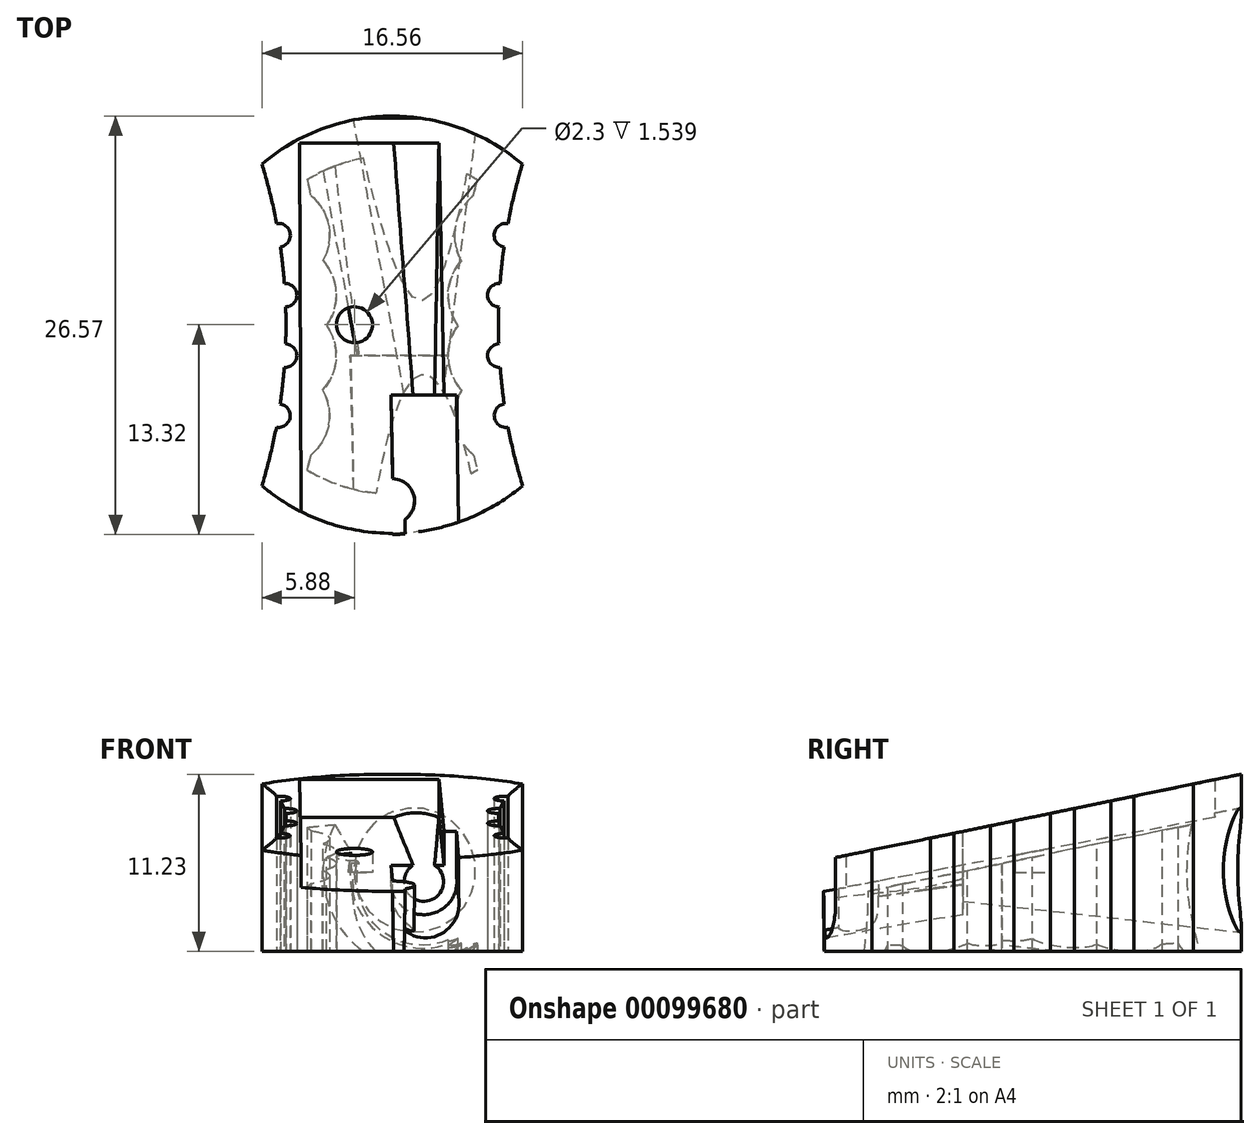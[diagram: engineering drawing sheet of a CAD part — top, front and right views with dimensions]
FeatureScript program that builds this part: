
annotation { "Feature Type Name" : "Feature", "Feature Type Description" : "" }
export const myFeature = defineFeature(function(context is Context, id is Id, definition is map)
    precondition{}
    {
        {
            var Q0;
            Q0=qCreatedBy(makeId("Top.planeOp"),FACE);
            var sketch = newSketch(context, id + "F0", { "sketchPlane" : qUnion([Q0])});
            skArc(sketch, "E0", {"start": v(-8.02, 9.64) * mm, "mid": v(-8.05, 9.61) * mm, "end": v(-8.09, 9.59) * mm, "construction": true});
            skArc(sketch, "E1", {"start": v(0, 13.25) * mm, "mid": v(-4.4, 12.46) * mm, "end": v(-8.27, 10.2) * mm});
            skArc(sketch, "E2", {"start": v(-8.28, -10.23) * mm, "mid": v(-6.76, 0.87) * mm, "end": v(-8.83, 11.88) * mm});
            skLineSegment(sketch, "E3", {"start": v(0, 27.52) * mm, "end": v(0, -29.67) * mm});
            skLineSegment(sketch, "E4", {"start": v(0, 13.25) * mm, "end": v(1.48, 13.25) * mm});
            skLineSegment(sketch, "E5", {"start": v(-7.8, 10.6) * mm, "end": v(-9.31, 9.42) * mm});
            skLineSegment(sketch, "E6", {"start": v(-9.2, 12.93) * mm, "end": v(-8.83, 11.88) * mm});
            skArc(sketch, "E7.trimOffspring", {"start": v(-8.28, -10.23) * mm, "mid": v(-4.4, -12.47) * mm, "end": v(0, -13.25) * mm});
            skLineSegment(sketch, "E8", {"start": v(0, -13.25) * mm, "end": v(1.48, -13.25) * mm});
            skCircle(sketch, "E9", {"center": v(-7.22, 5.69) * mm, "radius": 0.75 * mm});
            skCircle(sketch, "E10.1.0", {"center": v(-6.8, 1.88) * mm, "radius": 0.75 * mm});
            skCircle(sketch, "E10.2.0", {"center": v(-6.8, -1.96) * mm, "radius": 0.75 * mm});
            skCircle(sketch, "E10.3.0", {"center": v(-7.23, -5.77) * mm, "radius": 0.75 * mm});
            skLineSegment(sketch, "E10.anchor1", {"start": v(-41.75, 0) * mm, "end": v(-7.22, 5.69) * mm, "construction": true});
            skLineSegment(sketch, "E10.anchor2", {"start": v(-41.75, 0) * mm, "end": v(-7.23, -5.77) * mm, "construction": true});
            skSolve(sketch);
        }
        {
            var Q0;
            {var subQ3=sQuery(id+"F0.wireOp",EDGE,"E7.trimOffspring");Q0=makeQuery(id+"F0.imprint","IMPRINT",FACE,{"disambiguationData":[TD([[makeQuery(id+"F0.imprint","IMPRINT",EDGE,{"derivedFrom":subQ3}),1.0]])]});}
            extrude(context, id + "F1", {"entities" : qUnion([Q0]), "depth" : 11.23 * mm});
        }
        {
            var Q0;
            Q0=makeQuery(id+"F1.opExtrude","SWEPT_BODY",BODY,{"disambiguationData":[OSD([sQuery(id+"F0.wireOp",EDGE,"E1"),sQuery(id+"F0.wireOp",EDGE,"E2"),sQuery(id+"F0.wireOp",EDGE,"E3"),sQuery(id+"F0.wireOp",EDGE,"E7.trimOffspring")])]});
            var Q1;
            Q1=qCreatedBy(makeId("Right.planeOp"),FACE);
            mirror(context, id + "F2", {"operationType" : NewBodyOperationType.ADD, "entities" : qUnion([Q0]), "mirrorPlane" : qUnion([Q1])});
        }
        {
            var Q0;
            Q0=qCreatedBy(makeId("Right.planeOp"),FACE);
            var sketch = newSketch(context, id + "F3", { "sketchPlane" : qUnion([Q0])});
            skLineSegment(sketch, "E11", {"start": v(10.2, 10.63) * mm, "end": v(-10.23, 6.43) * mm});
            skLineSegment(sketch, "E12", {"start": v(15.76, 11.77) * mm, "end": v(-16.6, 5.12) * mm});
            skPoint(sketch, "E13.end.orphan", {"position": v(10.2, 0) * mm});
            skPoint(sketch, "E14.end.orphan", {"position": v(-10.23, 0) * mm});
            skLineSegment(sketch, "E15", {"start": v(15.76, 11.77) * mm, "end": v(15.76, 16.34) * mm});
            skLineSegment(sketch, "E16", {"start": v(15.76, 16.34) * mm, "end": v(-16.6, 16.34) * mm});
            skLineSegment(sketch, "E17", {"start": v(-16.6, 16.34) * mm, "end": v(-16.6, 5.12) * mm});
            skLineSegment(sketch, "E18", {"start": v(15.76, 11.77) * mm, "end": v(15.76, -3.68) * mm});
            skLineSegment(sketch, "E19", {"start": v(15.76, -3.68) * mm, "end": v(-16.6, -3.68) * mm});
            skLineSegment(sketch, "E20", {"start": v(-16.6, -3.68) * mm, "end": v(-16.6, 5.12) * mm});
            skSolve(sketch);
        }
        {
            var Q0;
            {var subQ0=sQuery(id+"F3.wireOp",EDGE,"E18");Q0=makeQuery(id+"F3.imprint","IMPRINT",FACE,{"disambiguationData":[TD([[makeQuery(id+"F3.imprint","IMPRINT",EDGE,{"derivedFrom":subQ0}),-1.0]])]});}
            extrude(context, id + "F4", {"entities" : qUnion([Q0]), "operationType" : NewBodyOperationType.INTERSECT, "depth" : 21.66 * mm, "symmetric" : true});
        }
        {
            var Q0;
            Q0=qCreatedBy(makeId("Right.planeOp"),FACE);
            cPlane(context, id + "F5", {"entities" : qUnion([Q0]), "cplaneType" : CPlaneType.OFFSET, "offset" : 3 * mm, "width" : 150 * mm, "height" : 150 * mm});
        }
        {
            var Q0;
            Q0=qCreatedBy(makeId("Front.planeOp"),FACE);
            cPlane(context, id + "F6", {"entities" : qUnion([Q0]), "cplaneType" : CPlaneType.OFFSET, "offset" : 13.25 * mm, "oppositeDirection" : true, "width" : 150 * mm, "height" : 150 * mm});
        }
        {
            var Q0;
            Q0=qCreatedBy(id+"F6.planeOp",FACE);
            var sketch = newSketch(context, id + "F7", { "sketchPlane" : qUnion([Q0])});
            skCircle(sketch, "E21", {"center": v(1.48, 5.16) * mm, "radius": 3.96 * mm});
            skLineSegment(sketch, "E22", {"start": v(5.44, 8.88) * mm, "end": v(5.44, 1.93) * mm});
            skLineSegment(sketch, "E23", {"start": v(6.15, 1.2) * mm, "end": v(-1.11, 1.2) * mm});
            skLineSegment(sketch, "E24", {"start": v(4.75, 9.13) * mm, "end": v(-1.65, 9.13) * mm});
            skSolve(sketch);
        }
        {
            var Q0;
            Q0=qCreatedBy(id+"F5.planeOp",FACE);
            var sketch = newSketch(context, id + "F8", { "sketchPlane" : qUnion([Q0])});
            skLineSegment(sketch, "E25", {"start": v(13.25, 8.83) * mm, "end": v(-16.57, 2.7) * mm});
            skLineSegment(sketch, "E26", {"start": v(13.25, 1.5) * mm, "end": v(-17.13, 5.21) * mm});
            skSolve(sketch);
        }
        {
            var Q0;
            Q0=qCreatedBy(id+"F6.planeOp",FACE);
            cPlane(context, id + "F9", {"entities" : qUnion([Q0]), "cplaneType" : CPlaneType.OFFSET, "offset" : 17.7 * mm, "width" : 150 * mm, "height" : 150 * mm});
        }
        {
            var Q0;
            Q0=qCreatedBy(id+"F9.planeOp",FACE);
            var sketch = newSketch(context, id + "F10", { "sketchPlane" : qUnion([Q0])});
            skCircle(sketch, "E27", {"center": v(2, 4.43) * mm, "radius": 1.25 * mm});
            skSolve(sketch);
        }
        {
            var Q1;
            Q1=makeQuery(id+"F7.imprint","IMPRINT",FACE,{"disambiguationData":[TD([[makeQuery(id+"F7.imprint","IMPRINT",EDGE,{"derivedFrom":sQuery(id+"F7.wireOp",EDGE,"E21")}),1.0]])]});
            var Q2;
            Q2 = qSketchRegion(id + "F10", true);
            loft(context, id + "F11", {"operationType" : NewBodyOperationType.REMOVE, "sheetProfilesArray" : [{ "sheetProfileEntities" : qUnion([Q1]) }, { "sheetProfileEntities" : qUnion([Q2]) }]});
        }
        {
            var Q0;
            Q0=qCreatedBy(id+"F6.planeOp",FACE);
            cPlane(context, id + "F12", {"entities" : qUnion([Q0]), "cplaneType" : CPlaneType.OFFSET, "offset" : 26.6 * mm, "width" : 150 * mm, "height" : 150 * mm});
        }
        {
            var Q0;
            Q0=qCreatedBy(id+"F9.planeOp",FACE);
            var sketch = newSketch(context, id + "F13", { "sketchPlane" : qUnion([Q0])});
            skCircle(sketch, "E28", {"center": v(2, 4.43) * mm, "radius": 2.1 * mm});
            skSolve(sketch);
        }
        {
            var Q0;
            Q0=qCreatedBy(id+"F12.planeOp",FACE);
            var sketch = newSketch(context, id + "F14", { "sketchPlane" : qUnion([Q0])});
            skCircle(sketch, "E29", {"center": v(2.18, 2.9) * mm, "radius": 2.1 * mm});
            skSolve(sketch);
        }
        {
            var Q1;
            Q1 = qSketchRegion(id + "F13", true);
            var Q2;
            Q2 = qSketchRegion(id + "F14", true);
            loft(context, id + "F15", {"operationType" : NewBodyOperationType.REMOVE, "sheetProfilesArray" : [{ "sheetProfileEntities" : qUnion([Q1]) }, { "sheetProfileEntities" : qUnion([Q2]) }]});
        }
        {
            var Q0;
            {var subQ0=makeQuery(id+"F1.opExtrude","CAP_FACE",FACE,{"disambiguationData":[OSD([sQuery(id+"F0.wireOp",EDGE,"E1"),sQuery(id+"F0.wireOp",EDGE,"E2"),sQuery(id+"F0.wireOp",EDGE,"E3"),sQuery(id+"F0.wireOp",EDGE,"E7.trimOffspring")])],"isStart":true});Q0=makeQuery(id+"F2.boolean.opBoolean","MERGE",FACE,{"derivedFrom":[subQ0,makeQuery(id+"F2.opPattern","COPY",FACE,{"derivedFrom":subQ0,"instanceName":"1"})]});}
            shell(context, id + "F16", {"entities" : qUnion([Q0]), "thickness" : 2.5 * mm});
        }
        {
            var Q0;
            Q0=qCreatedBy(id+"F12.planeOp",FACE);
            var sketch = newSketch(context, id + "F17", { "sketchPlane" : qUnion([Q0])});
            skLineSegment(sketch, "E30", {"start": v(-5.78, 3.79) * mm, "end": v(3.46, 3.79) * mm});
            skLineSegment(sketch, "E31", {"start": v(3.46, 3.79) * mm, "end": v(3.46, 5.79) * mm});
            skLineSegment(sketch, "E32", {"start": v(3.46, 5.79) * mm, "end": v(-5.78, 5.79) * mm});
            skLineSegment(sketch, "E33", {"start": v(-5.78, 3.79) * mm, "end": v(-5.78, 5.79) * mm});
            skSolve(sketch);
        }
        {
            var Q0;
            Q0=qCreatedBy(id+"F6.planeOp",FACE);
            cPlane(context, id + "F18", {"entities" : qUnion([Q0]), "cplaneType" : CPlaneType.OFFSET, "offset" : 1.7 * mm, "width" : 150 * mm, "height" : 150 * mm});
        }
        {
            var Q0;
            Q0=qCreatedBy(id+"F18.planeOp",FACE);
            var sketch = newSketch(context, id + "F19", { "sketchPlane" : qUnion([Q0])});
            skLineSegment(sketch, "E34", {"start": v(2.97, 10.9) * mm, "end": v(-5.87, 10.9) * mm});
            skLineSegment(sketch, "E35", {"start": v(-5.87, 10.9) * mm, "end": v(-5.87, 8.5) * mm});
            skLineSegment(sketch, "E36", {"start": v(-5.87, 8.5) * mm, "end": v(2.97, 8.5) * mm});
            skLineSegment(sketch, "E37", {"start": v(2.97, 8.5) * mm, "end": v(2.97, 10.9) * mm});
            skSolve(sketch);
        }
        {
            var Q0;
            Q0=qCreatedBy(id+"F9.planeOp",FACE);
            var sketch = newSketch(context, id + "F20", { "sketchPlane" : qUnion([Q0])});
            skLineSegment(sketch, "E38.bottom", {"start": v(-0.08, 4.24) * mm, "end": v(4.1, 4.24) * mm});
            skLineSegment(sketch, "E38.top", {"start": v(-0.08, 10.02) * mm, "end": v(4.1, 10.02) * mm});
            skLineSegment(sketch, "E38.left", {"start": v(-0.08, 10.02) * mm, "end": v(-0.08, 4.24) * mm});
            skLineSegment(sketch, "E38.right", {"start": v(4.1, 10.02) * mm, "end": v(4.1, 4.24) * mm});
            skSolve(sketch);
        }
        {
            var Q0;
            Q0=qCreatedBy(id+"F12.planeOp",FACE);
            var sketch = newSketch(context, id + "F21", { "sketchPlane" : qUnion([Q0])});
            skLineSegment(sketch, "E39.bottom", {"start": v(0.08, 9.94) * mm, "end": v(4.23, 9.94) * mm});
            skLineSegment(sketch, "E39.top", {"start": v(0.08, 3) * mm, "end": v(4.23, 3) * mm});
            skLineSegment(sketch, "E39.left", {"start": v(0.08, 3) * mm, "end": v(0.08, 9.94) * mm});
            skLineSegment(sketch, "E39.right", {"start": v(4.23, 3) * mm, "end": v(4.23, 9.94) * mm});
            skSolve(sketch);
        }
        {
            var Q1;
            Q1 = qSketchRegion(id + "F21", true);
            var Q2;
            Q2 = qSketchRegion(id + "F20", true);
            loft(context, id + "F22", {"operationType" : NewBodyOperationType.REMOVE, "sheetProfilesArray" : [{ "sheetProfileEntities" : qUnion([Q1]) }, { "sheetProfileEntities" : qUnion([Q2]) }]});
        }
        {
            var Q0;
            Q0=qCreatedBy(makeId("Top.planeOp"),FACE);
            var sketch = newSketch(context, id + "F23", { "sketchPlane" : qUnion([Q0])});
            skArc(sketch, "E40", {"start": v(0.76, -12.33) * mm, "mid": v(1.3, -10.81) * mm, "end": v(0, -9.85) * mm});
            skLineSegment(sketch, "E41.right", {"start": v(0.76, -12.33) * mm, "end": v(0.76, -13.23) * mm});
            skArc(sketch, "E42", {"start": v(0.08, -13.25) * mm, "mid": v(0.42, -13.24) * mm, "end": v(0.76, -13.23) * mm});
            skLineSegment(sketch, "E43", {"start": v(0.08, -13.25) * mm, "end": v(0, -9.85) * mm});
            skSolve(sketch);
        }
        {
            var Q0;
            Q0 = qSketchRegion(id + "F23", true);
            extrude(context, id + "F24", {"entities" : qUnion([Q0]), "operationType" : NewBodyOperationType.ADD, "depth" : 4.8 * mm, "hasDraft" : true, "draftAngle" : 1 * degree});
        }
        {
            var Q1;
            Q1 = qSketchRegion(id + "F19", true);
            var Q2;
            Q2 = qSketchRegion(id + "F17", true);
            loft(context, id + "F25", {"operationType" : NewBodyOperationType.REMOVE, "sheetProfilesArray" : [{ "sheetProfileEntities" : qUnion([Q1]) }, { "sheetProfileEntities" : qUnion([Q2]) }]});
        }
        {
            var Q0;
            Q0=qCreatedBy(makeId("Top.planeOp"),FACE);
            var sketch = newSketch(context, id + "F26", { "sketchPlane" : qUnion([Q0])});
            skCircle(sketch, "E44", {"center": v(-2.4, 0) * mm, "radius": 1.15 * mm});
            skSolve(sketch);
        }
        {
            var Q0;
            Q0 = qSketchRegion(id + "F26", true);
            var Q1;
            Q1=makeQuery(id+"F25.boolean.opBoolean","COPY",FACE,{"disambiguationData":[OD(1.0)],"derivedFrom":makeQuery(id+"F25.opLoft","SWEPT_FACE",FACE,{"disambiguationData":[OSD([sQuery(id+"F17.wireOp",EDGE,"E30"),sQuery(id+"F17.wireOp",EDGE,"E31"),sQuery(id+"F17.wireOp",EDGE,"E33"),sQuery(id+"F19.wireOp",EDGE,"E35"),sQuery(id+"F19.wireOp",EDGE,"E36"),sQuery(id+"F19.wireOp",EDGE,"E37")])]})});
            extrude(context, id + "F27", {"entities" : qUnion([Q0, Q1]), "operationType" : NewBodyOperationType.REMOVE, "depth" : 22 * mm, "hasSecondDirection" : true, "secondDirectionOppositeDirection" : false, "secondDirectionDepth" : 5 * mm});
        }
    });
